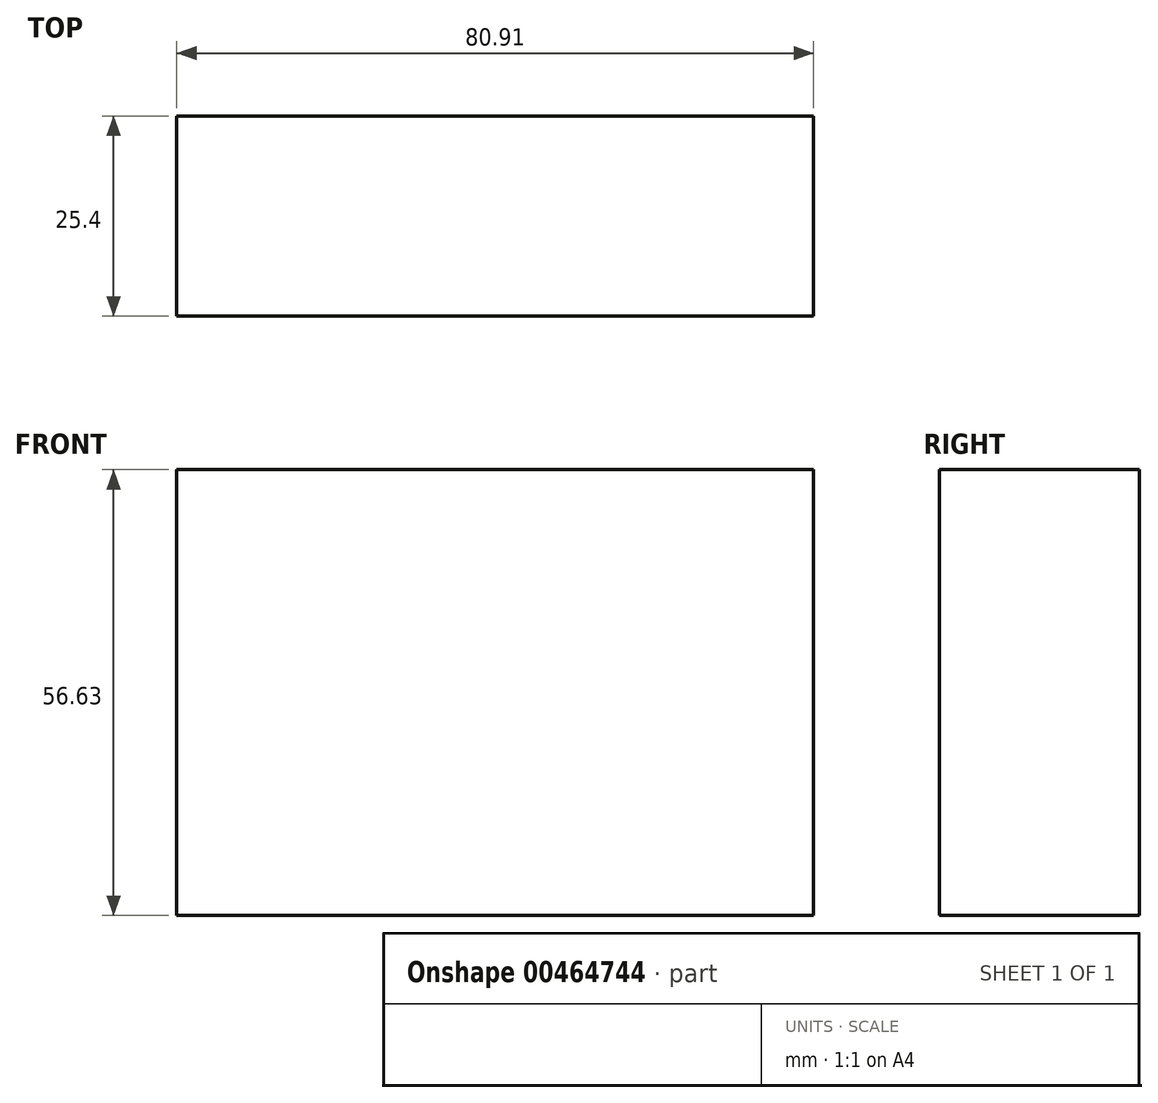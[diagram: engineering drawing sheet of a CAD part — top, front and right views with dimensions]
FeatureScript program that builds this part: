
annotation { "Feature Type Name" : "Feature", "Feature Type Description" : "" }
export const myFeature = defineFeature(function(context is Context, id is Id, definition is map)
    precondition{}
    {
        {
            var Q0;
            Q0=qCreatedBy(makeId("Front.planeOp"),FACE);
            var sketch = newSketch(context, id + "F0", { "sketchPlane" : qUnion([Q0])});
            skLineSegment(sketch, "E0.bottom", {"start": v(44.4, -27.6) * mm, "end": v(-36.51, -27.6) * mm});
            skLineSegment(sketch, "E0.top", {"start": v(44.4, 29.04) * mm, "end": v(-36.51, 29.04) * mm});
            skLineSegment(sketch, "E0.left", {"start": v(44.4, -27.6) * mm, "end": v(44.4, 29.04) * mm});
            skLineSegment(sketch, "E0.right", {"start": v(-36.51, -27.6) * mm, "end": v(-36.51, 29.04) * mm});
            skSolve(sketch);
        }
        {
            var Q0;
            Q0=makeQuery(id+"F0.imprint","IMPRINT",FACE,{"disambiguationData":[TD([[makeQuery(id+"F0.imprint","IMPRINT",EDGE,{"derivedFrom":sQuery(id+"F0.wireOp",EDGE,"E0.bottom")}),-1.0]])]});
            extrude(context, id + "F1", {"entities" : qUnion([Q0]), "depth" : 25.4 * mm});
        }
    });
